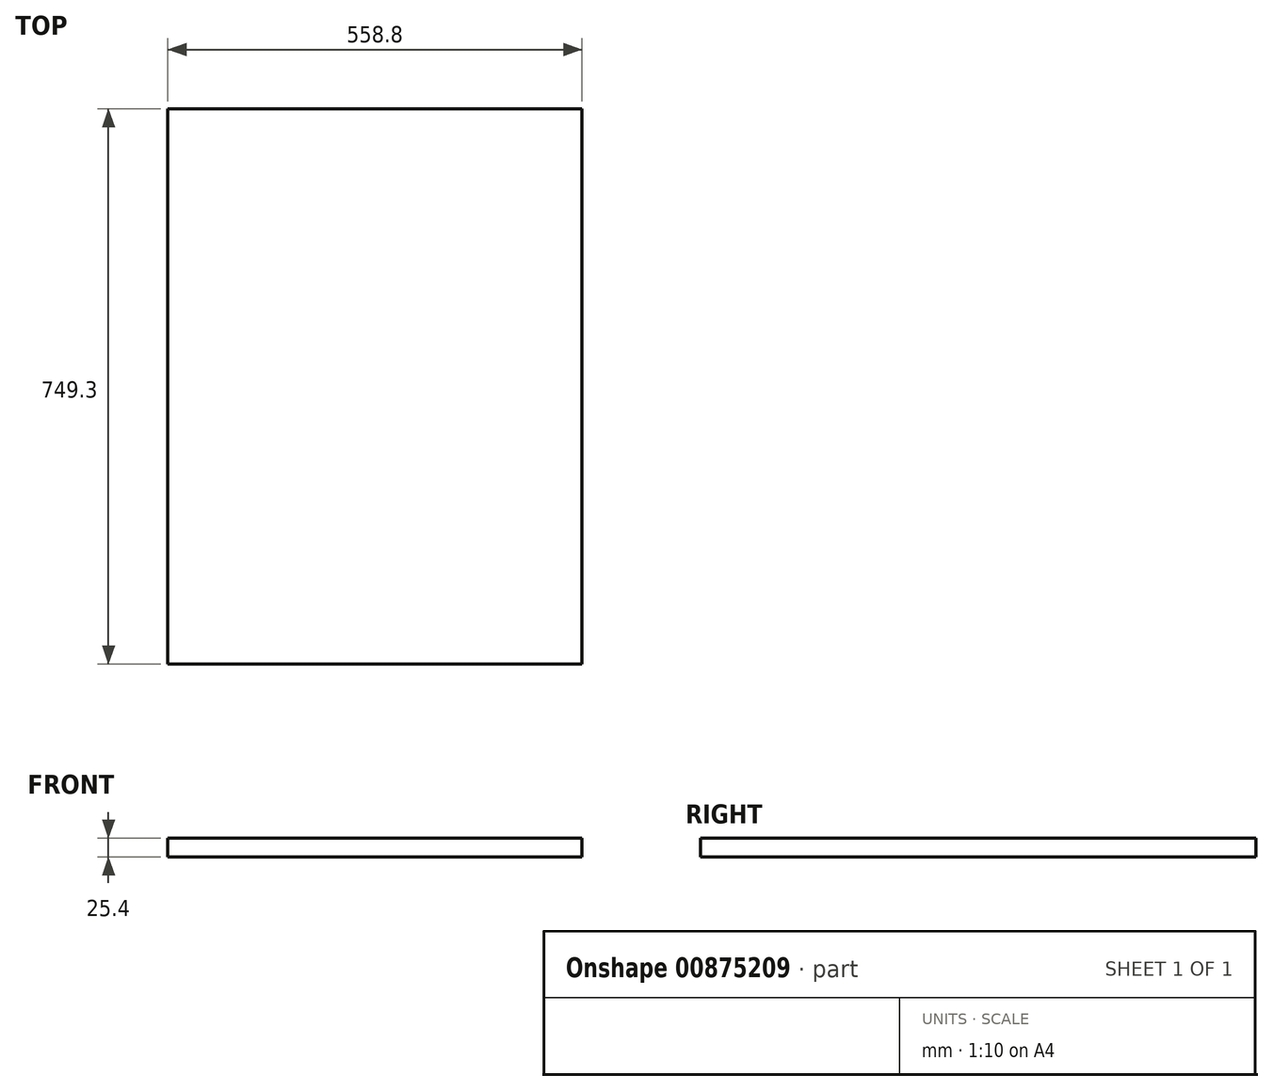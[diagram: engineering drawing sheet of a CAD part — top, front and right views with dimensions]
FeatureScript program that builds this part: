
annotation { "Feature Type Name" : "Feature", "Feature Type Description" : "" }
export const myFeature = defineFeature(function(context is Context, id is Id, definition is map)
    precondition{}
    {
        {
            var Q0;
            Q0=qCreatedBy(makeId("Top.planeOp"),FACE);
            var sketch = newSketch(context, id + "F0", { "sketchPlane" : qUnion([Q0])});
            skLineSegment(sketch, "E0.bottom", {"start": v(-279.4, 374.65) * mm, "end": v(279.4, 374.65) * mm});
            skLineSegment(sketch, "E0.top", {"start": v(-279.4, -374.65) * mm, "end": v(279.4, -374.65) * mm});
            skLineSegment(sketch, "E0.left", {"start": v(-279.4, 374.65) * mm, "end": v(-279.4, -374.65) * mm});
            skLineSegment(sketch, "E0.right", {"start": v(279.4, 374.65) * mm, "end": v(279.4, -374.65) * mm});
            skPoint(sketch, "E0.middle", {"position": v(0, 0) * mm});
            skSolve(sketch);
        }
        {
            var Q0;
            Q0=makeQuery(id+"F0.imprint","IMPRINT",FACE,{"disambiguationData":[TD([[makeQuery(id+"F0.imprint","IMPRINT",EDGE,{"derivedFrom":sQuery(id+"F0.wireOp",EDGE,"E0.bottom")}),-1.0]])]});
            extrude(context, id + "F1", {"entities" : qUnion([Q0]), "depth" : 25.4 * mm, "offsetDistance" : 25.4 * mm});
        }
    });
